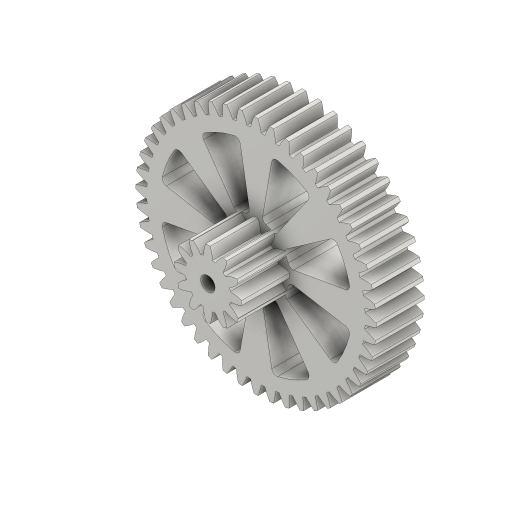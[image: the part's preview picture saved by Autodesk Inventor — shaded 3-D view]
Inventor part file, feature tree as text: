
AUTODESK INVENTOR PART (.ipt)
format: ipt  version: 2024 (Build 280153000, 153)  size: 740,352 bytes
history: native  units: mm (DEFAULTED — no unit token found)
features: extrude x6, sketch x6, plane x3, other x3, fillet x1
ambient origin geometry x8: Origin, YZ Plane, XZ Plane, XY Plane, X Axis, Y Axis, Z Axis, Center Point
bodies: Solid1 (feature_tree)
feature tree (19):
  extrude  "Extrusion1"  Depth=20.0mm TaperAngle=0.0deg
  plane  "Work Plane2"
  plane  "Work Plane8"
  plane  "Work Plane9"
  other  "Spur Gear"
  extrude  "Extrusion2"  Depth=10.0mm TaperAngle=0.0deg
  extrude  "Extrusion3"  Depth=0.654498mm TaperAngle=0.0deg
  extrude  "Extrusion4"  TaperAngle=0.0deg  [1 undecoded]
  extrude  "Extrusion5"  Depth=60.0mm
  extrude  "Extrusion6"  Depth=20.0mm TaperAngle=0.0deg
  fillet  "Fillet1"  Radius=8.0mm
  sketch  "Sketch1"  dims[d0=100.0mm d1=20.0mm d2=0.0mm]
  other  "Srf1"
  sketch  "Sketch3"  dims[d3=96.0mm d4=10.0mm d5=0.0mm]
  sketch  "Sketch4"  dims[d16=60.0mm d17=0.0mm d34=0.654498mm]
  sketch  "Sketch6"  dims[d39=0.0mm d41=0.0mm]
  sketch  "Sketch7"  dims[d43=60.0mm d46=60.0mm]
  sketch  "Sketch8"  dims[d47=0.0mm d48=0.0mm d49=20.0mm d50=0.0mm d51=8.0mm d52=20.0mm d53=0.0mm d54=20.0mm d55=0.0mm d56=6.0mm d57=25.0mm d58=0.0mm d59=80.0mm d60=1.745329mm d61=6.108652mm d62=9.599311mm d63=1.745329mm d64=6.108652mm d65=9.599311mm d66=25.0mm d67=0.0mm d68=2.0mm]
  other  "Pitch Diameter"
note: 1 required parameter value undecoded (feature->parameter linkage not recoverable at this tier; creation-order binding heuristic only, values carry confidence <= 0.55)
